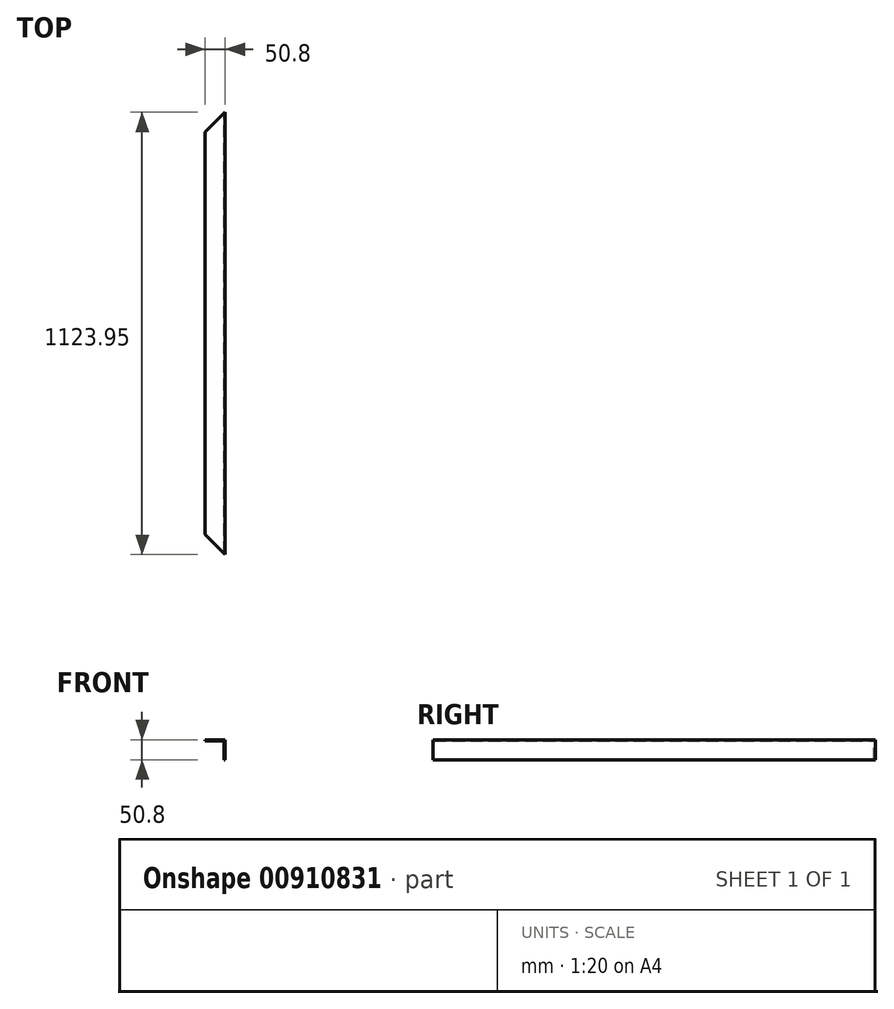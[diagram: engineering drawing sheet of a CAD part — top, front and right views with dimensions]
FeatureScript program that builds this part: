
annotation { "Feature Type Name" : "Feature", "Feature Type Description" : "" }
export const myFeature = defineFeature(function(context is Context, id is Id, definition is map)
    precondition{}
    {
        {
            var Q0;
            Q0=qCreatedBy(makeId("Front.planeOp"),FACE);
            var sketch = newSketch(context, id + "F0", { "sketchPlane" : qUnion([Q0])});
            skLineSegment(sketch, "E0", {"start": v(0, 0) * mm, "end": v(50.8, 0) * mm});
            skLineSegment(sketch, "E1", {"start": v(50.8, 0) * mm, "end": v(50.8, -50.8) * mm});
            skLineSegment(sketch, "E2.0", {"start": v(47.62, -3.18) * mm, "end": v(47.63, -50.8) * mm});
            skLineSegment(sketch, "E2.1", {"start": v(0, -3.18) * mm, "end": v(47.62, -3.18) * mm});
            skLineSegment(sketch, "E3", {"start": v(0, 0) * mm, "end": v(0, -3.18) * mm});
            skLineSegment(sketch, "E4", {"start": v(50.8, -50.8) * mm, "end": v(47.63, -50.8) * mm});
            skSolve(sketch);
        }
        {
            var Q0;
            Q0 = qSketchRegion(id + "F0", true);
            extrude(context, id + "F1", {"entities" : qUnion([Q0]), "flatOperationType" : FlatOperationType.REMOVE, "depth" : 1123.95 * mm, "offsetDistance" : 25.4 * mm, "domain" : OperationDomain.MODEL});
        }
        {
            var Q0;
            Q0=makeQuery(id+"F1.opExtrude","SWEPT_FACE",FACE,{"disambiguationData":[OSD([sQuery(id+"F0.wireOp",EDGE,"E0")])]});
            var sketch = newSketch(context, id + "F2", { "sketchPlane" : qUnion([Q0])});
            skLineSegment(sketch, "E5", {"start": v(50.8, 0) * mm, "end": v(0, -50.8) * mm});
            skLineSegment(sketch, "E6", {"start": v(0, -50.8) * mm, "end": v(0, 0) * mm});
            skLineSegment(sketch, "E7", {"start": v(0, 0) * mm, "end": v(50.8, 0) * mm});
            skLineSegment(sketch, "E8", {"start": v(50.8, -1123.95) * mm, "end": v(0, -1073.15) * mm});
            skLineSegment(sketch, "E9", {"start": v(0, -1073.15) * mm, "end": v(0, -1123.95) * mm});
            skLineSegment(sketch, "E10", {"start": v(0, -1123.95) * mm, "end": v(50.8, -1123.95) * mm});
            skSolve(sketch);
        }
        {
            var Q0;
            Q0 = qSketchRegion(id + "F2", true);
            extrude(context, id + "F3", {"entities" : qUnion([Q0]), "operationType" : NewBodyOperationType.REMOVE, "endBound" : BoundingType.THROUGH_ALL, "oppositeDirection" : true, "depth" : 25.4 * mm, "offsetDistance" : 25.4 * mm});
        }
    });
